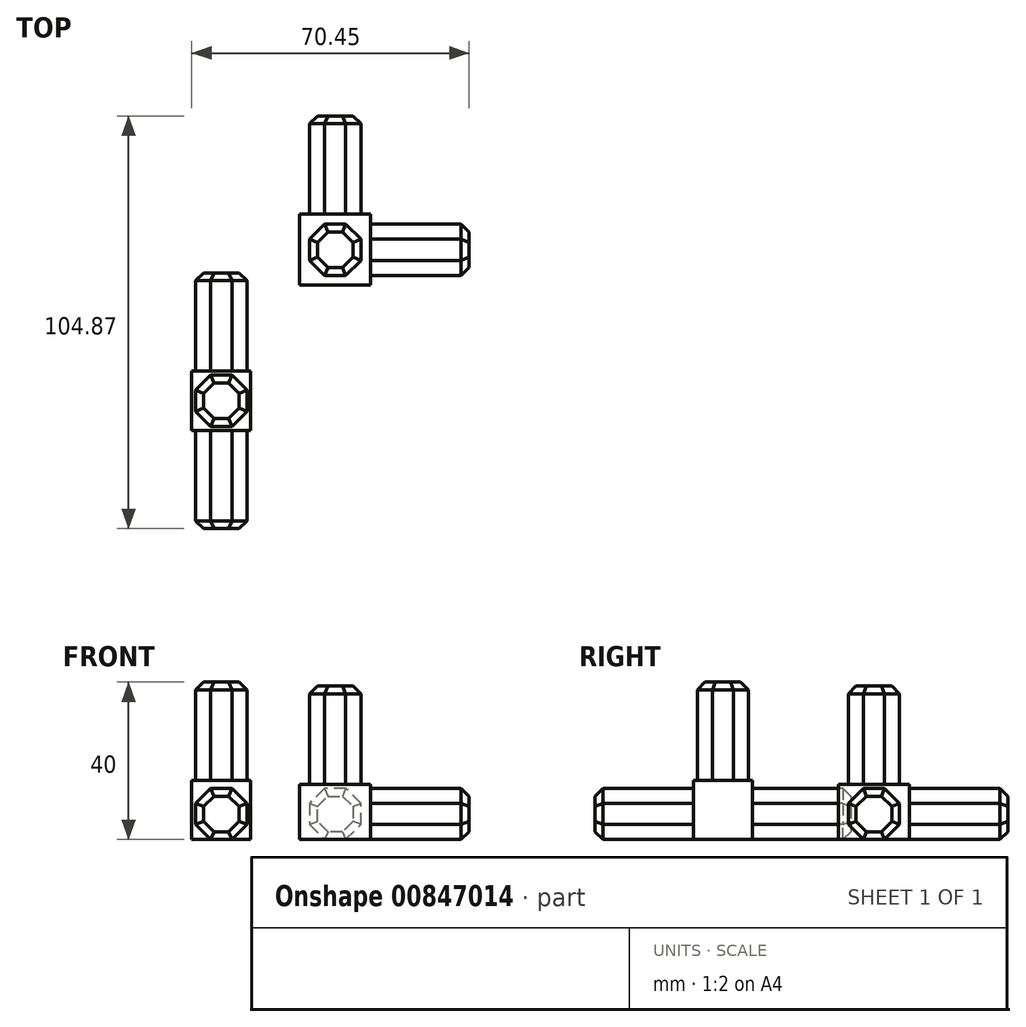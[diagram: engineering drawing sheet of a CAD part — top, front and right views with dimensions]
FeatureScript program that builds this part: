
annotation { "Feature Type Name" : "Feature", "Feature Type Description" : "" }
export const myFeature = defineFeature(function(context is Context, id is Id, definition is map)
    precondition{}
    {
        {
            var Q0;
            Q0=qCreatedBy(makeId("Top.planeOp"),FACE);
            var sketch = newSketch(context, id + "F0", { "sketchPlane" : qUnion([Q0])});
            skLineSegment(sketch, "E0.bottom", {"start": v(0, 0) * mm, "end": v(18, 0) * mm});
            skLineSegment(sketch, "E0.top", {"start": v(0, 18) * mm, "end": v(18, 18) * mm});
            skLineSegment(sketch, "E0.left", {"start": v(0, 0) * mm, "end": v(0, 18) * mm});
            skLineSegment(sketch, "E0.right", {"start": v(18, 0) * mm, "end": v(18, 18) * mm});
            skSolve(sketch);
        }
        {
            var Q0;
            Q0 = qSketchRegion(id + "F0", true);
            extrude(context, id + "F1", {"entities" : qUnion([Q0]), "depth" : 14 * mm, "offsetDistance" : 25 * mm});
        }
        {
            var Q0;
            Q0=makeQuery(id+"F1.opExtrude","SWEPT_FACE",FACE,{"disambiguationData":[OSD([sQuery(id+"F0.wireOp",EDGE,"E0.right")])]});
            var sketch = newSketch(context, id + "F2", { "sketchPlane" : qUnion([Q0])});
            skCircle(sketch, "E1.cCircle", {"center": v(9, 6.51) * mm, "radius": 7.05 * mm, "construction": true});
            skLineSegment(sketch, "E1.0", {"start": v(11.7, 0) * mm, "end": v(6.3, 0) * mm});
            skLineSegment(sketch, "E1.1", {"start": v(6.3, 0) * mm, "end": v(2.49, 3.82) * mm});
            skLineSegment(sketch, "E1.2", {"start": v(2.49, 3.82) * mm, "end": v(2.49, 9.21) * mm});
            skLineSegment(sketch, "E1.3", {"start": v(2.49, 9.21) * mm, "end": v(6.3, 13.03) * mm});
            skLineSegment(sketch, "E1.4", {"start": v(6.3, 13.03) * mm, "end": v(11.7, 13.03) * mm});
            skLineSegment(sketch, "E1.5", {"start": v(11.7, 13.03) * mm, "end": v(15.51, 9.21) * mm});
            skLineSegment(sketch, "E1.6", {"start": v(15.51, 9.21) * mm, "end": v(15.51, 3.82) * mm});
            skLineSegment(sketch, "E1.7", {"start": v(15.51, 3.82) * mm, "end": v(11.7, 0) * mm});
            skSolve(sketch);
        }
        {
            var Q0;
            Q0=makeQuery(id+"F1.opExtrude","SWEPT_FACE",FACE,{"disambiguationData":[OSD([sQuery(id+"F0.wireOp",EDGE,"E0.top")])]});
            var sketch = newSketch(context, id + "F3", { "sketchPlane" : qUnion([Q0])});
            skCircle(sketch, "E2.cCircle", {"center": v(-9, 6.51) * mm, "radius": 7.05 * mm, "construction": true});
            skLineSegment(sketch, "E2.0", {"start": v(-6.3, 0) * mm, "end": v(-11.7, 0) * mm});
            skLineSegment(sketch, "E2.1", {"start": v(-11.7, 0) * mm, "end": v(-15.51, 3.82) * mm});
            skLineSegment(sketch, "E2.2", {"start": v(-15.51, 3.82) * mm, "end": v(-15.51, 9.21) * mm});
            skLineSegment(sketch, "E2.3", {"start": v(-15.51, 9.21) * mm, "end": v(-11.7, 13.03) * mm});
            skLineSegment(sketch, "E2.4", {"start": v(-11.7, 13.03) * mm, "end": v(-6.3, 13.03) * mm});
            skLineSegment(sketch, "E2.5", {"start": v(-6.3, 13.03) * mm, "end": v(-2.49, 9.21) * mm});
            skLineSegment(sketch, "E2.6", {"start": v(-2.49, 9.21) * mm, "end": v(-2.49, 3.82) * mm});
            skLineSegment(sketch, "E2.7", {"start": v(-2.49, 3.82) * mm, "end": v(-6.3, 0) * mm});
            skSolve(sketch);
        }
        {
            var Q0;
            Q0=makeQuery(id+"F1.opExtrude","CAP_FACE",FACE,{"disambiguationData":[OSD([sQuery(id+"F0.wireOp",EDGE,"E0.bottom"),sQuery(id+"F0.wireOp",EDGE,"E0.top"),sQuery(id+"F0.wireOp",EDGE,"E0.left"),sQuery(id+"F0.wireOp",EDGE,"E0.right")])],"isStart":false});
            var sketch = newSketch(context, id + "F4", { "sketchPlane" : qUnion([Q0])});
            skCircle(sketch, "E3.cCircle", {"center": v(9, 9) * mm, "radius": 7.05 * mm, "construction": true});
            skLineSegment(sketch, "E3.0", {"start": v(6.3, 15.51) * mm, "end": v(11.7, 15.51) * mm});
            skLineSegment(sketch, "E3.1", {"start": v(11.7, 15.51) * mm, "end": v(15.51, 11.7) * mm});
            skLineSegment(sketch, "E3.2", {"start": v(15.51, 11.7) * mm, "end": v(15.51, 6.3) * mm});
            skLineSegment(sketch, "E3.3", {"start": v(15.51, 6.3) * mm, "end": v(11.7, 2.49) * mm});
            skLineSegment(sketch, "E3.4", {"start": v(11.7, 2.49) * mm, "end": v(6.3, 2.49) * mm});
            skLineSegment(sketch, "E3.5", {"start": v(6.3, 2.49) * mm, "end": v(2.49, 6.3) * mm});
            skLineSegment(sketch, "E3.6", {"start": v(2.49, 6.3) * mm, "end": v(2.49, 11.7) * mm});
            skLineSegment(sketch, "E3.7", {"start": v(2.49, 11.7) * mm, "end": v(6.3, 15.51) * mm});
            skSolve(sketch);
        }
        {
            var Q0;
            Q0 = qSketchRegion(id + "F2", true);
            extrude(context, id + "F5", {"entities" : qUnion([Q0]), "operationType" : NewBodyOperationType.ADD, "depth" : 25 * mm, "offsetDistance" : 25 * mm});
        }
        {
            var Q0;
            Q0 = qSketchRegion(id + "F3", true);
            extrude(context, id + "F6", {"entities" : qUnion([Q0]), "operationType" : NewBodyOperationType.ADD, "depth" : 25 * mm, "offsetDistance" : 25 * mm});
        }
        {
            var Q0;
            Q0 = qSketchRegion(id + "F4", true);
            extrude(context, id + "F7", {"entities" : qUnion([Q0]), "operationType" : NewBodyOperationType.ADD, "depth" : 25 * mm, "offsetDistance" : 25 * mm});
        }
        {
            var Q0;
            Q0=makeQuery(id+"F7.opExtrude","CAP_FACE",FACE,{"disambiguationData":[OSD([sQuery(id+"F4.wireOp",EDGE,"E3.0"),sQuery(id+"F4.wireOp",EDGE,"E3.1"),sQuery(id+"F4.wireOp",EDGE,"E3.2"),sQuery(id+"F4.wireOp",EDGE,"E3.3"),sQuery(id+"F4.wireOp",EDGE,"E3.4"),sQuery(id+"F4.wireOp",EDGE,"E3.5"),sQuery(id+"F4.wireOp",EDGE,"E3.6"),sQuery(id+"F4.wireOp",EDGE,"E3.7")])],"isStart":false});
            var Q1;
            Q1=makeQuery(id+"F5.opExtrude","CAP_FACE",FACE,{"disambiguationData":[OSD([sQuery(id+"F2.wireOp",EDGE,"E1.0"),sQuery(id+"F2.wireOp",EDGE,"E1.1"),sQuery(id+"F2.wireOp",EDGE,"E1.2"),sQuery(id+"F2.wireOp",EDGE,"E1.3"),sQuery(id+"F2.wireOp",EDGE,"E1.4"),sQuery(id+"F2.wireOp",EDGE,"E1.5"),sQuery(id+"F2.wireOp",EDGE,"E1.6"),sQuery(id+"F2.wireOp",EDGE,"E1.7")])],"isStart":false});
            var Q2;
            Q2=makeQuery(id+"F6.opExtrude","CAP_FACE",FACE,{"disambiguationData":[OSD([sQuery(id+"F3.wireOp",EDGE,"E2.0"),sQuery(id+"F3.wireOp",EDGE,"E2.1"),sQuery(id+"F3.wireOp",EDGE,"E2.2"),sQuery(id+"F3.wireOp",EDGE,"E2.3"),sQuery(id+"F3.wireOp",EDGE,"E2.4"),sQuery(id+"F3.wireOp",EDGE,"E2.5"),sQuery(id+"F3.wireOp",EDGE,"E2.6"),sQuery(id+"F3.wireOp",EDGE,"E2.7")])],"isStart":false});
            chamfer(context, id + "F8", {"entities" : qUnion([Q0, Q1, Q2]), "width" : 2 * mm, "tangentPropagation" : true});
        }
        {
            var Q0;
            Q0=qCreatedBy(makeId("Top.planeOp"),FACE);
            var sketch = newSketch(context, id + "F9", { "sketchPlane" : qUnion([Q0])});
            skLineSegment(sketch, "E4.bottom", {"start": v(-27.45, -36.87) * mm, "end": v(-12.45, -36.87) * mm});
            skLineSegment(sketch, "E4.top", {"start": v(-27.45, -21.87) * mm, "end": v(-12.45, -21.87) * mm});
            skLineSegment(sketch, "E4.left", {"start": v(-27.45, -36.87) * mm, "end": v(-27.45, -21.87) * mm});
            skLineSegment(sketch, "E4.right", {"start": v(-12.45, -36.87) * mm, "end": v(-12.45, -21.87) * mm});
            skSolve(sketch);
        }
        {
            var Q0;
            Q0 = qSketchRegion(id + "F9", true);
            extrude(context, id + "F10", {"entities" : qUnion([Q0]), "depth" : 15 * mm, "offsetDistance" : 25 * mm});
        }
        {
            var Q0;
            Q0=makeQuery(id+"F10.opExtrude","SWEPT_FACE",FACE,{"disambiguationData":[OSD([sQuery(id+"F9.wireOp",EDGE,"E4.bottom")])]});
            var sketch = newSketch(context, id + "F11", { "sketchPlane" : qUnion([Q0])});
            skCircle(sketch, "E5.cCircle", {"center": v(-19.95, 6.51) * mm, "radius": 7.05 * mm, "construction": true});
            skLineSegment(sketch, "E5.0", {"start": v(-17.25, 0) * mm, "end": v(-22.64, 0) * mm});
            skLineSegment(sketch, "E5.1", {"start": v(-22.64, 0) * mm, "end": v(-26.46, 3.82) * mm});
            skLineSegment(sketch, "E5.2", {"start": v(-26.46, 3.82) * mm, "end": v(-26.46, 9.21) * mm});
            skLineSegment(sketch, "E5.3", {"start": v(-26.46, 9.21) * mm, "end": v(-22.64, 13.03) * mm});
            skLineSegment(sketch, "E5.4", {"start": v(-22.64, 13.03) * mm, "end": v(-17.25, 13.03) * mm});
            skLineSegment(sketch, "E5.5", {"start": v(-17.25, 13.03) * mm, "end": v(-13.43, 9.21) * mm});
            skLineSegment(sketch, "E5.6", {"start": v(-13.43, 9.21) * mm, "end": v(-13.43, 3.82) * mm});
            skLineSegment(sketch, "E5.7", {"start": v(-13.43, 3.82) * mm, "end": v(-17.25, 0) * mm});
            skSolve(sketch);
        }
        {
            var Q0;
            Q0=makeQuery(id+"F10.opExtrude","SWEPT_FACE",FACE,{"disambiguationData":[OSD([sQuery(id+"F9.wireOp",EDGE,"E4.top")])]});
            var sketch = newSketch(context, id + "F12", { "sketchPlane" : qUnion([Q0])});
            skCircle(sketch, "E6.cCircle", {"center": v(19.95, 6.51) * mm, "radius": 7.05 * mm, "construction": true});
            skLineSegment(sketch, "E6.0", {"start": v(22.64, 0) * mm, "end": v(17.25, 0) * mm});
            skLineSegment(sketch, "E6.1", {"start": v(17.25, 0) * mm, "end": v(13.43, 3.82) * mm});
            skLineSegment(sketch, "E6.2", {"start": v(13.43, 3.82) * mm, "end": v(13.43, 9.21) * mm});
            skLineSegment(sketch, "E6.3", {"start": v(13.43, 9.21) * mm, "end": v(17.25, 13.03) * mm});
            skLineSegment(sketch, "E6.4", {"start": v(17.25, 13.03) * mm, "end": v(22.64, 13.03) * mm});
            skLineSegment(sketch, "E6.5", {"start": v(22.64, 13.03) * mm, "end": v(26.46, 9.21) * mm});
            skLineSegment(sketch, "E6.6", {"start": v(26.46, 9.21) * mm, "end": v(26.46, 3.82) * mm});
            skLineSegment(sketch, "E6.7", {"start": v(26.46, 3.82) * mm, "end": v(22.64, 0) * mm});
            skSolve(sketch);
        }
        {
            var Q0;
            Q0=makeQuery(id+"F10.opExtrude","CAP_FACE",FACE,{"disambiguationData":[OSD([sQuery(id+"F9.wireOp",EDGE,"E4.bottom"),sQuery(id+"F9.wireOp",EDGE,"E4.top"),sQuery(id+"F9.wireOp",EDGE,"E4.left"),sQuery(id+"F9.wireOp",EDGE,"E4.right")])],"isStart":false});
            var sketch = newSketch(context, id + "F13", { "sketchPlane" : qUnion([Q0])});
            skCircle(sketch, "E7.cCircle", {"center": v(-19.95, -29.37) * mm, "radius": 7.05 * mm, "construction": true});
            skLineSegment(sketch, "E7.0", {"start": v(-17.25, -35.88) * mm, "end": v(-22.64, -35.88) * mm});
            skLineSegment(sketch, "E7.1", {"start": v(-22.64, -35.88) * mm, "end": v(-26.46, -32.07) * mm});
            skLineSegment(sketch, "E7.2", {"start": v(-26.46, -32.07) * mm, "end": v(-26.46, -26.67) * mm});
            skLineSegment(sketch, "E7.3", {"start": v(-26.46, -26.67) * mm, "end": v(-22.64, -22.86) * mm});
            skLineSegment(sketch, "E7.4", {"start": v(-22.64, -22.86) * mm, "end": v(-17.25, -22.86) * mm});
            skLineSegment(sketch, "E7.5", {"start": v(-17.25, -22.86) * mm, "end": v(-13.43, -26.67) * mm});
            skLineSegment(sketch, "E7.6", {"start": v(-13.43, -26.67) * mm, "end": v(-13.43, -32.07) * mm});
            skLineSegment(sketch, "E7.7", {"start": v(-13.43, -32.07) * mm, "end": v(-17.25, -35.88) * mm});
            skSolve(sketch);
        }
        {
            var Q0;
            Q0 = qSketchRegion(id + "F11", true);
            extrude(context, id + "F14", {"entities" : qUnion([Q0]), "operationType" : NewBodyOperationType.ADD, "depth" : 25 * mm, "offsetDistance" : 25 * mm});
        }
        {
            var Q0;
            Q0 = qSketchRegion(id + "F12", true);
            extrude(context, id + "F15", {"entities" : qUnion([Q0]), "operationType" : NewBodyOperationType.ADD, "depth" : 25 * mm, "offsetDistance" : 25 * mm});
        }
        {
            var Q0;
            Q0 = qSketchRegion(id + "F13", true);
            extrude(context, id + "F16", {"entities" : qUnion([Q0]), "operationType" : NewBodyOperationType.ADD, "depth" : 25 * mm, "offsetDistance" : 25 * mm});
        }
        {
            var Q0;
            Q0=makeQuery(id+"F14.opExtrude","CAP_FACE",FACE,{"disambiguationData":[OSD([sQuery(id+"F11.wireOp",EDGE,"E5.0"),sQuery(id+"F11.wireOp",EDGE,"E5.1"),sQuery(id+"F11.wireOp",EDGE,"E5.2"),sQuery(id+"F11.wireOp",EDGE,"E5.3"),sQuery(id+"F11.wireOp",EDGE,"E5.4"),sQuery(id+"F11.wireOp",EDGE,"E5.5"),sQuery(id+"F11.wireOp",EDGE,"E5.6"),sQuery(id+"F11.wireOp",EDGE,"E5.7")])],"isStart":false});
            var Q1;
            Q1=makeQuery(id+"F16.opExtrude","CAP_FACE",FACE,{"disambiguationData":[OSD([sQuery(id+"F13.wireOp",EDGE,"E7.0"),sQuery(id+"F13.wireOp",EDGE,"E7.1"),sQuery(id+"F13.wireOp",EDGE,"E7.2"),sQuery(id+"F13.wireOp",EDGE,"E7.3"),sQuery(id+"F13.wireOp",EDGE,"E7.4"),sQuery(id+"F13.wireOp",EDGE,"E7.5"),sQuery(id+"F13.wireOp",EDGE,"E7.6"),sQuery(id+"F13.wireOp",EDGE,"E7.7")])],"isStart":false});
            var Q2;
            Q2=makeQuery(id+"F15.opExtrude","CAP_FACE",FACE,{"disambiguationData":[OSD([sQuery(id+"F12.wireOp",EDGE,"E6.0"),sQuery(id+"F12.wireOp",EDGE,"E6.1"),sQuery(id+"F12.wireOp",EDGE,"E6.2"),sQuery(id+"F12.wireOp",EDGE,"E6.3"),sQuery(id+"F12.wireOp",EDGE,"E6.4"),sQuery(id+"F12.wireOp",EDGE,"E6.5"),sQuery(id+"F12.wireOp",EDGE,"E6.6"),sQuery(id+"F12.wireOp",EDGE,"E6.7")])],"isStart":false});
            chamfer(context, id + "F17", {"entities" : qUnion([Q0, Q1, Q2]), "width" : 2 * mm, "tangentPropagation" : true});
        }
    });
